# Revit family: Intersan Modus
name_source: partatom
category: Plumbing Fixtures
revit_build: Autodesk Revit 2017 (Build: 20170816_0615(x64)
units: mm (PartAtom-declared; Revit-internal decimal feet)

## family parameters
Always vertical = Yes
Cut with Voids When Loaded = No
OmniClass Number = 23.45.05.14.14
OmniClass Title = Sinks/Lavatories
Part Type = Normal
Room Calculation Point = No
Round Connector Dimension = Use Diameter
Shared = No
Work Plane-Based = No

## types (9) — shared parameters
CW Connection = Yes
Drain Diameter = 1 1/2"
HW Connection = Yes
Manufacturer = Intersan
Material = Anti-microbial Solid Surface and Stainless Steel
Model = Modus
Standard Conformance = CSA B45.5-11/IAPMO Z124-2011 - IAPMO IGC156
Supply Cold Diameter = 1/2"
Supply Hot Diameter = 1/2"
Unit Depth = 22 1/8"
Warranty = 5 years on material - 1 year on faucets
Waste Connection = Yes
Water Usage = 0.35 gpm/user if Intersan Faucets

## per-type parameters (varying)
| type | Apron Height | Unit Height | Unit Width |
| Modus 20 - No Skirt | 5" | 8 3/4" | 20" |
| Modus 20 - No Skirt - Canada | 4 1/8" | 8 3/4" | 20" |
| Modus 20 - Skirt | 5" | 15" | 20" |
| Modus 25 - No Skirt | 5" | 8 3/4" | 25" |
| Modus 25 - No Skirt - Canada | 4 1/8" | 8 3/4" | 25" |
| Modus 25 - Skirt | 5" | 15" | 25" |
| Modus 50 - No Skirt | 5" | 8 3/4" | 50" |
| Modus 50 - No Skirt - Canada | 4 1/8"" | 8 3/4" | 50" |
| Modus 50 - Skirt | 5" | 15" | 50" |

type visibility flags (boolean, named after types; folded from table):
- Modus 20 - No Skirt: Yes: Modus 20 - No Skirt
- Modus 20 - No Skirt - Canada: Yes: Modus 20 - No Skirt - Canada
- Modus 20 - Skirt: Yes: Modus 20 - Skirt
- Modus 25 - No Skirt: Yes: Modus 25 - No Skirt
- Modus 25 - No Skirt - Canada: Yes: Modus 25 - No Skirt Canada
- Modus 25 - Skirt: Yes: Modus 25 - Skirt
- Modus 50 - No Skirt: Yes: Modus 50 - No Skirt
- Modus 50 - No Skirt - Canada: Yes: Modus 50 - No Skirt Canada
- Modus 50 - Skirt: Yes: Modus 50 - Skirt

## geometry (parser evidence)
native form markers: Sweep x1
no freeform markers — native parametric forms only
